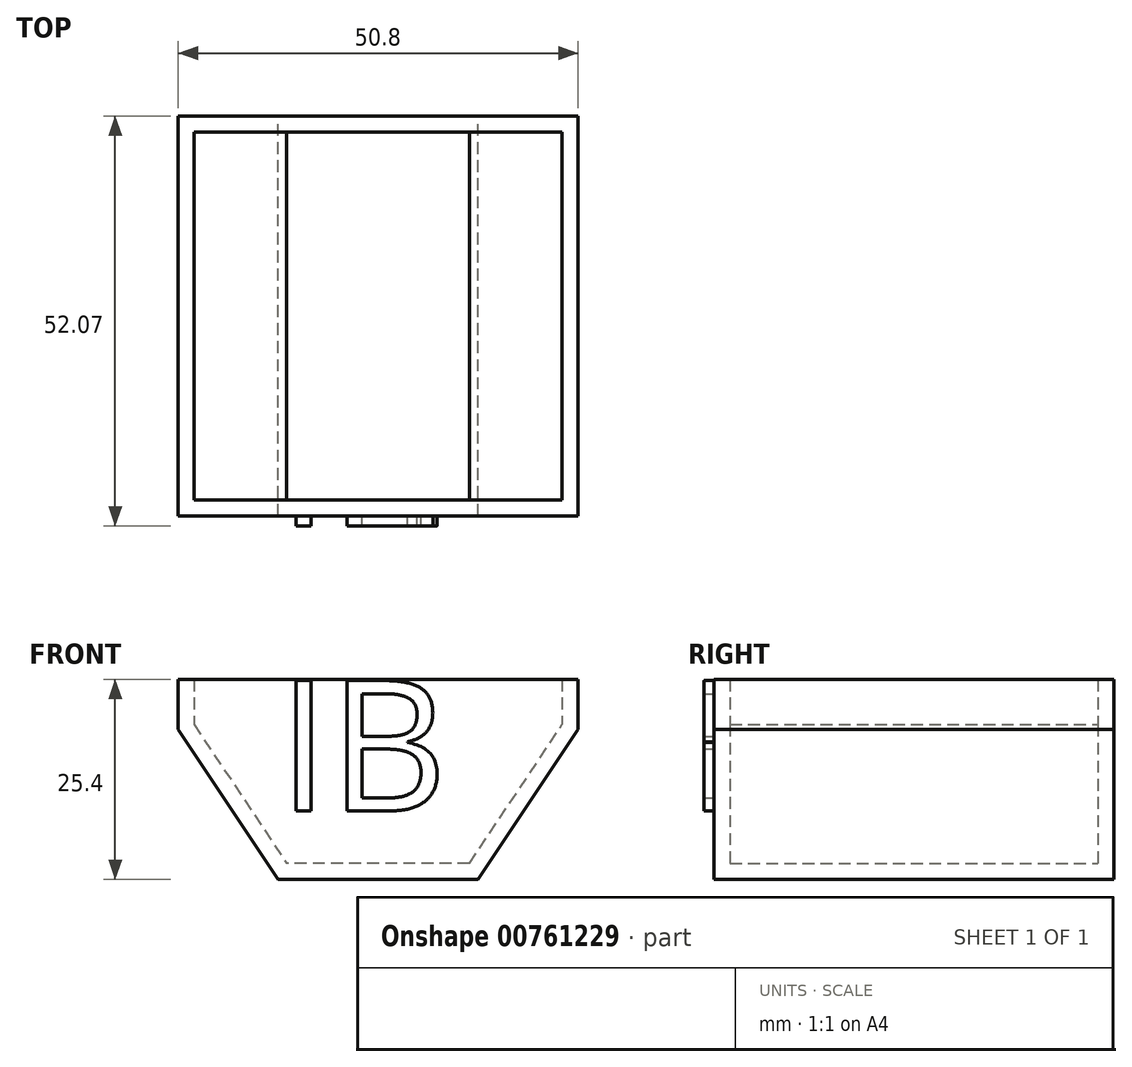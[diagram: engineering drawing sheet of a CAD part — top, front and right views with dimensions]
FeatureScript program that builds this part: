
annotation { "Feature Type Name" : "Feature", "Feature Type Description" : "" }
export const myFeature = defineFeature(function(context is Context, id is Id, definition is map)
    precondition{}
    {
        {
            var Q0;
            Q0=qCreatedBy(makeId("Front.planeOp"),FACE);
            var sketch = newSketch(context, id + "F0", { "sketchPlane" : qUnion([Q0])});
            skLineSegment(sketch, "E0", {"start": v(-111.98, 16.68) * mm, "end": v(-61.18, 16.68) * mm});
            skLineSegment(sketch, "E1", {"start": v(-86.58, 16.68) * mm, "end": v(-86.58, -8.72) * mm});
            skLineSegment(sketch, "E2", {"start": v(-86.58, -8.72) * mm, "end": v(-99.28, -8.72) * mm});
            skLineSegment(sketch, "E3", {"start": v(-111.98, 16.68) * mm, "end": v(-111.98, 10.33) * mm});
            skLineSegment(sketch, "E4", {"start": v(-61.18, 16.68) * mm, "end": v(-61.18, 10.33) * mm});
            skLineSegment(sketch, "E5", {"start": v(-111.98, 10.33) * mm, "end": v(-99.28, -8.72) * mm});
            skLineSegment(sketch, "E6", {"start": v(-86.58, -8.72) * mm, "end": v(-73.88, -8.72) * mm});
            skLineSegment(sketch, "E7", {"start": v(-73.88, -8.72) * mm, "end": v(-61.18, 10.33) * mm});
            skSolve(sketch);
        }
        {
            var Q0;
            {var subQ1=sQuery(id+"F0.wireOp",EDGE,"E1");Q0=makeQuery(id+"F0.imprint","IMPRINT",FACE,{"disambiguationData":[TD([[makeQuery(id+"F0.imprint","IMPRINT",EDGE,{"derivedFrom":subQ1}),-1.0]])]});}
            var Q1;
            {var subQ1=sQuery(id+"F0.wireOp",EDGE,"E1");Q1=makeQuery(id+"F0.imprint","IMPRINT",FACE,{"disambiguationData":[TD([[makeQuery(id+"F0.imprint","IMPRINT",EDGE,{"derivedFrom":subQ1}),1.0]])]});}
            extrude(context, id + "F1", {"entities" : qUnion([Q0, Q1]), "depth" : 50.8 * mm, "offsetDistance" : 25.4 * mm});
        }
        {
            var Q0;
            Q0=makeQuery(id+"F1.opExtrude","SWEPT_FACE",FACE,{"disambiguationData":[OSD([sQuery(id+"F0.wireOp",EDGE,"E0")])]});
            shell(context, id + "F2", {"entities" : qUnion([Q0]), "thickness" : 2.03 * mm});
        }
        {
            var Q0;
            Q0=makeQuery(id+"F1.opExtrude","CAP_FACE",FACE,{"disambiguationData":[OSD([sQuery(id+"F0.wireOp",EDGE,"E0"),sQuery(id+"F0.wireOp",EDGE,"E2"),sQuery(id+"F0.wireOp",EDGE,"E3"),sQuery(id+"F0.wireOp",EDGE,"E4"),sQuery(id+"F0.wireOp",EDGE,"E5"),sQuery(id+"F0.wireOp",EDGE,"E6"),sQuery(id+"F0.wireOp",EDGE,"E7")])],"isStart":false});
            var sketch = newSketch(context, id + "F3", { "sketchPlane" : qUnion([Q0])});
            skText(sketch, "E8", { "text": "IB", "fontName": "OpenSans-Regular.ttf"});
            const initialGuessF3  = {"E8": [-0.09928, 0, 1, 0, 0.01668]};
            skSetInitialGuess(sketch, initialGuessF3);
            skSolve(sketch);
        }
        {
            var Q0;
            Q0 = qSketchRegion(id + "F3", true);
            extrude(context, id + "F4", {"entities" : qUnion([Q0]), "operationType" : NewBodyOperationType.ADD, "depth" : 1.27 * mm, "offsetDistance" : 25.4 * mm});
        }
    });
